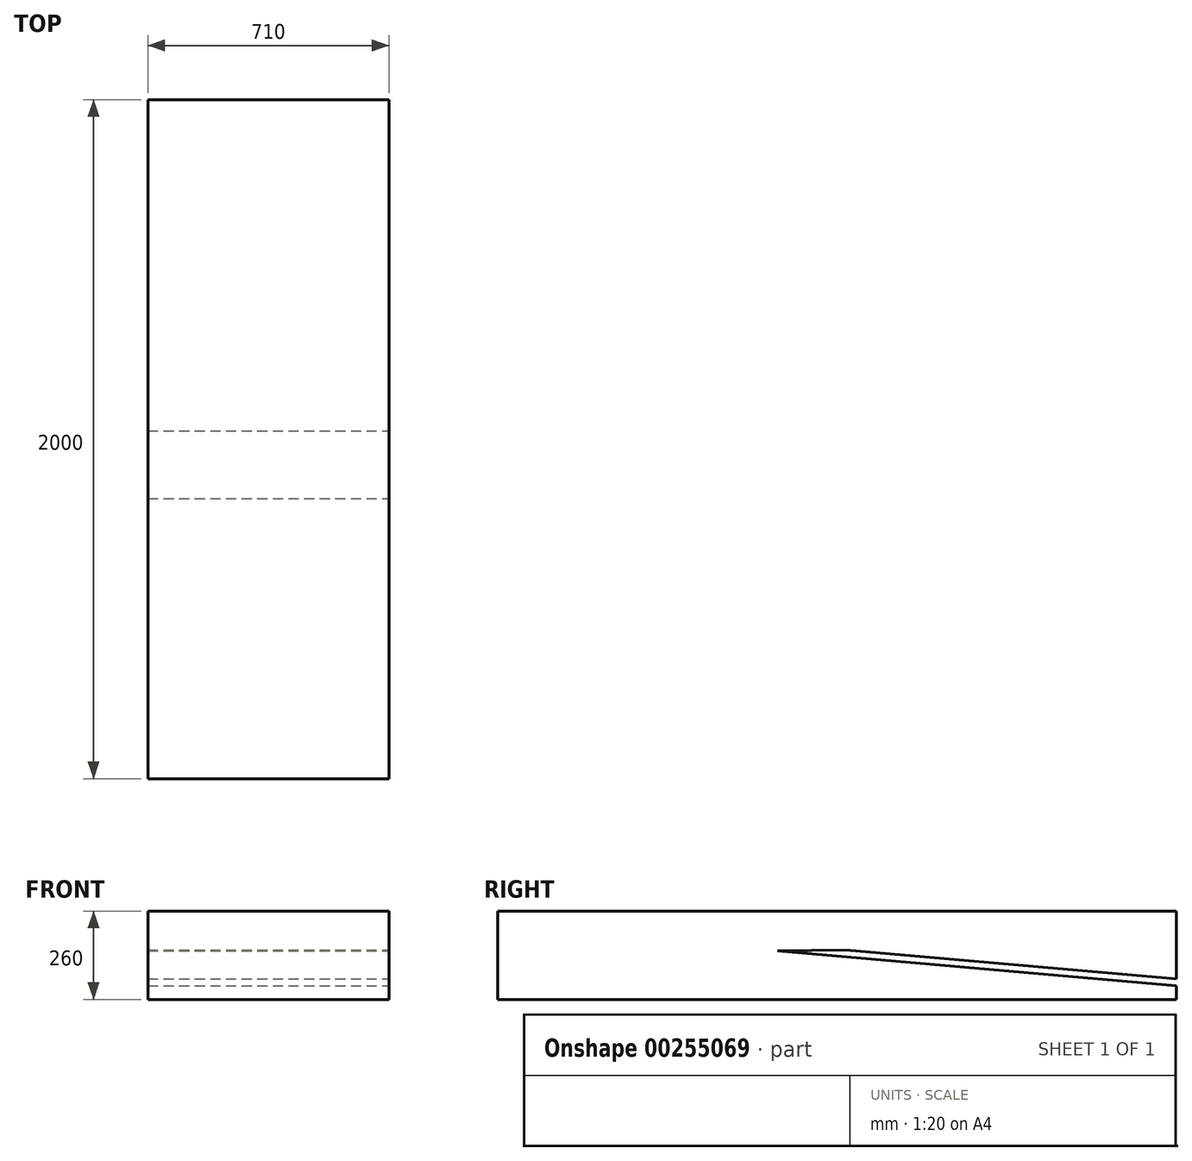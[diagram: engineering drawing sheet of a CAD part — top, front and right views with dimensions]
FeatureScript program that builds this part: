
annotation { "Feature Type Name" : "Feature", "Feature Type Description" : "" }
export const myFeature = defineFeature(function(context is Context, id is Id, definition is map)
    precondition{}
    {
        {
            var Q0;
            Q0=qCreatedBy(makeId("Front.planeOp"),FACE);
            var sketch = newSketch(context, id + "F0", { "sketchPlane" : qUnion([Q0])});
            skLineSegment(sketch, "E0.bottom", {"start": v(355, -130) * mm, "end": v(-355, -130) * mm});
            skLineSegment(sketch, "E0.top", {"start": v(355, 130) * mm, "end": v(-355, 130) * mm});
            skLineSegment(sketch, "E0.left", {"start": v(355, -130) * mm, "end": v(355, 130) * mm});
            skLineSegment(sketch, "E0.right", {"start": v(-355, -130) * mm, "end": v(-355, 130) * mm});
            skPoint(sketch, "E0.middle", {"position": v(0, 0) * mm});
            skSolve(sketch);
        }
        {
            var Q0;
            Q0=makeQuery(id+"F0.imprint","IMPRINT",FACE,{"disambiguationData":[TD([[makeQuery(id+"F0.imprint","IMPRINT",EDGE,{"derivedFrom":sQuery(id+"F0.wireOp",EDGE,"E0.bottom")}),-1.0]])]});
            extrude(context, id + "F1", {"entities" : qUnion([Q0]), "depth" : 2000 * mm});
        }
        {
            var Q0;
            Q0=makeQuery(id+"F1.opExtrude","SWEPT_FACE",FACE,{"disambiguationData":[OSD([sQuery(id+"F0.wireOp",EDGE,"E0.left")])]});
            var sketch = newSketch(context, id + "F2", { "sketchPlane" : qUnion([Q0])});
            skLineSegment(sketch, "E1", {"start": v(0, -70) * mm, "end": v(-974.77, 15.28) * mm});
            skLineSegment(sketch, "E2", {"start": v(-974.77, 15.28) * mm, "end": v(-1174.77, 12.78) * mm});
            skLineSegment(sketch, "E3", {"start": v(-1174.77, 12.78) * mm, "end": v(0, -90) * mm});
            skLineSegment(sketch, "E4", {"start": v(0, -90) * mm, "end": v(0, -70) * mm});
            skSolve(sketch);
        }
        {
            var Q0;
            Q0 = qSketchRegion(id + "F2", true);
            extrude(context, id + "F3", {"entities" : qUnion([Q0]), "operationType" : NewBodyOperationType.REMOVE, "endBound" : BoundingType.THROUGH_ALL, "oppositeDirection" : true, "depth" : 25 * mm});
        }
    });
